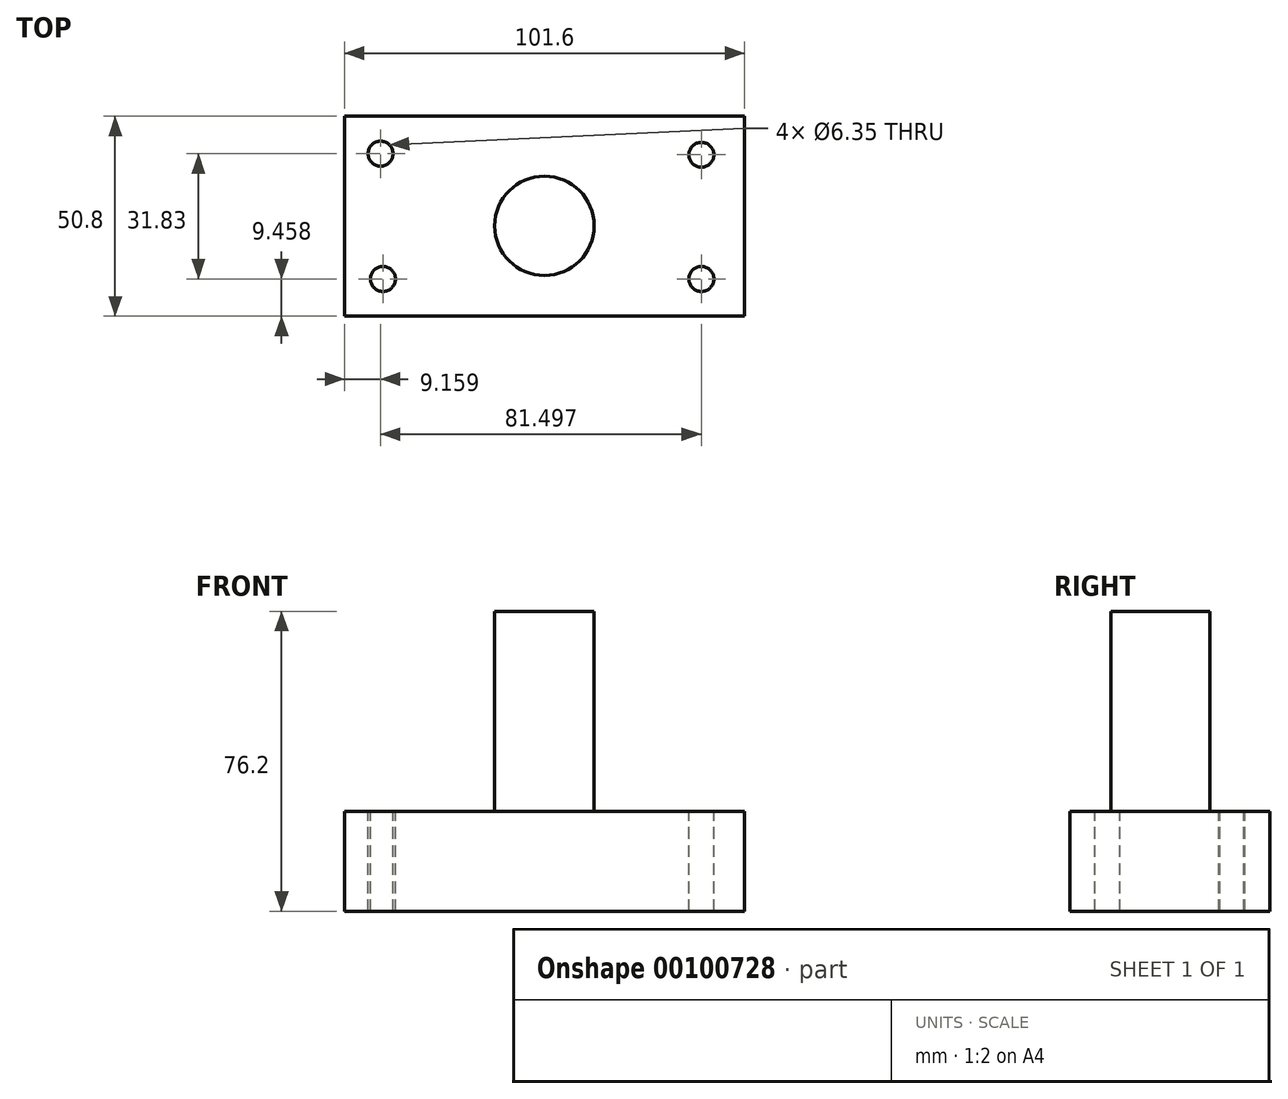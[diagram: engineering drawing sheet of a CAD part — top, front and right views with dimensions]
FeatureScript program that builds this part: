
annotation { "Feature Type Name" : "Feature", "Feature Type Description" : "" }
export const myFeature = defineFeature(function(context is Context, id is Id, definition is map)
    precondition{}
    {
        {
            var Q0;
            Q0=qCreatedBy(makeId("Top.planeOp"),FACE);
            var sketch = newSketch(context, id + "F0", { "sketchPlane" : qUnion([Q0])});
            skLineSegment(sketch, "E0.bottom", {"start": v(-50.8, 27.85) * mm, "end": v(50.8, 27.85) * mm});
            skLineSegment(sketch, "E0.top", {"start": v(-50.8, -22.95) * mm, "end": v(50.8, -22.95) * mm});
            skLineSegment(sketch, "E0.left", {"start": v(-50.8, 27.85) * mm, "end": v(-50.8, -22.95) * mm});
            skLineSegment(sketch, "E0.right", {"start": v(50.8, 27.85) * mm, "end": v(50.8, -22.95) * mm});
            skPoint(sketch, "E0.middle", {"position": v(0, 2.45) * mm});
            skSolve(sketch);
        }
        {
            var Q0;
            Q0 = qSketchRegion(id + "F0", true);
            var Q1;
            Q1=makeQuery(id+"F0.imprint","IMPRINT",FACE,{"disambiguationData":[TD([[makeQuery(id+"F0.imprint","IMPRINT",EDGE,{"derivedFrom":sQuery(id+"F0.wireOp",EDGE,"E0.bottom")}),-1.0]])]});
            extrude(context, id + "F1", {"entities" : qUnion([Q0, Q1]), "depth" : 25.4 * mm});
        }
        {
            var Q0;
            Q0=makeQuery(id+"F1.opExtrude","CAP_FACE",FACE,{"disambiguationData":[OSD([sQuery(id+"F0.wireOp",EDGE,"E0.bottom"),sQuery(id+"F0.wireOp",EDGE,"E0.top"),sQuery(id+"F0.wireOp",EDGE,"E0.left"),sQuery(id+"F0.wireOp",EDGE,"E0.right")])],"isStart":false});
            var sketch = newSketch(context, id + "F2", { "sketchPlane" : qUnion([Q0])});
            skCircle(sketch, "E1", {"center": v(-41.64, 18.34) * mm, "radius": 6.35 * mm});
            skCircle(sketch, "E2", {"center": v(-41.05, -13.5) * mm, "radius": 6.35 * mm});
            skCircle(sketch, "E3", {"center": v(39.86, 18.04) * mm, "radius": 6.35 * mm});
            skCircle(sketch, "E4", {"center": v(39.86, -13.5) * mm, "radius": 6.35 * mm});
            skSolve(sketch);
        }
        {
            var Q0;
            Q0=makeQuery(id+"F2.imprint","IMPRINT",FACE,{"disambiguationData":[TD([[makeQuery(id+"F2.imprint","IMPRINT",EDGE,{"derivedFrom":sQuery(id+"F2.wireOp",EDGE,"E1")}),-1.0]])]});
            var sketch = newSketch(context, id + "F3", { "sketchPlane" : qUnion([Q0])});
            skCircle(sketch, "E5", {"center": v(0, 0) * mm, "radius": 12.63 * mm});
            skSolve(sketch);
        }
        {
            var Q0;
            Q0=makeQuery(id+"F3.imprint","IMPRINT",FACE,{"disambiguationData":[TD([[makeQuery(id+"F3.imprint","IMPRINT",EDGE,{"derivedFrom":sQuery(id+"F3.wireOp",EDGE,"E5")}),1.0]])]});
            extrude(context, id + "F4", {"entities" : qUnion([Q0]), "operationType" : NewBodyOperationType.ADD, "depth" : 50.8 * mm});
        }
        {
            var Q0;
            Q0=sQuery(id+"F2.wireOp",VERTEX,"E2.center");
            var Q1;
            Q1=sQuery(id+"F2.wireOp",VERTEX,"E4.center");
            var Q2;
            Q2=sQuery(id+"F2.wireOp",VERTEX,"E3.center");
            var Q3;
            Q3=sQuery(id+"F2.wireOp",VERTEX,"E1.center");
            var Q4;
            Q4=makeQuery(id+"F1.opExtrude","SWEPT_BODY",BODY,{"disambiguationData":[OSD([sQuery(id+"F0.wireOp",EDGE,"E0.bottom"),sQuery(id+"F0.wireOp",EDGE,"E0.top"),sQuery(id+"F0.wireOp",EDGE,"E0.left"),sQuery(id+"F0.wireOp",EDGE,"E0.right")])]});
            hole(context, id + "F5", {"style" : HoleStyle.SIMPLE, "endStyle" : HoleEndStyle.THROUGH, "holeDiameter" : 6.35 * mm, "locations" : qUnion([Q0, Q1, Q2, Q3]), "scope" : qUnion([Q4]), "isTappedThrough" : true});
        }
    });
